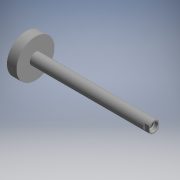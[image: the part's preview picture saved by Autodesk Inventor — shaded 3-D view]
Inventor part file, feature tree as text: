
AUTODESK INVENTOR PART (.ipt)
format: ipt  version: 2017.3 (Build 213256000, 256)  size: 137,216 bytes
history: native  units: mm (DEFAULTED — no unit token found)
features: other x21, sketch x4, revolve x3, extrude x1, thread x1
ambient origin geometry x8: Origin, YZ Plane, XZ Plane, XY Plane, X Axis, Y Axis, Z Axis, Center Point
bodies: Solid1 (feature_tree)
feature tree (30):
  revolve  "Revolution1"  Angle=360.0deg
  revolve  "Revolution2"  Angle=360.0deg
  extrude  "Extrusion1"  TaperAngle=0.0deg  [1 undecoded]
  revolve  "Revolution3"  [1 undecoded]
  thread  "Thread1"  [1 undecoded]
  other  "FDT_PIRODACC_F1_XY"
  other  "FDT_PIRODACC_F1_YZ"
  other  "FDT_PIRODACC_F1_ZX"
  other  "FDT_PIRODACC_F1_X"
  other  "FDT_PIRODACC_F1_Y"
  other  "FDT_PIRODACC_F1_Z"
  other  "FDT_PIRODACC_F1_Center"
  other  "NUT1_XY"
  other  "NUT1_YZ"
  other  "NUT1_ZX"
  other  "NUT1_X"
  other  "NUT1_Y"
  other  "NUT1_Z"
  other  "NUT1_Center"
  other  "PISTON_XY"
  other  "PISTON_YZ"
  other  "PISTON_ZX"
  other  "PISTON_X"
  other  "PISTON_Y"
  other  "PISTON_Z"
  other  "PISTON_Center"
  sketch  "Sketch_1"  dims[d0=360.0deg d1=360.0deg]
  sketch  "Sketch_11"  dims[d5=12.0235mm d6=0.0mm d7=0.0mm d8=0.0mm]
  sketch  "Sketch_20"
  sketch  "Sketch_2"  dims[d2=24.0mm d3=0.0mm d4=360.0deg]
note: 3 required parameter values undecoded (feature->parameter linkage not recoverable at this tier; creation-order binding heuristic only, values carry confidence <= 0.55)
